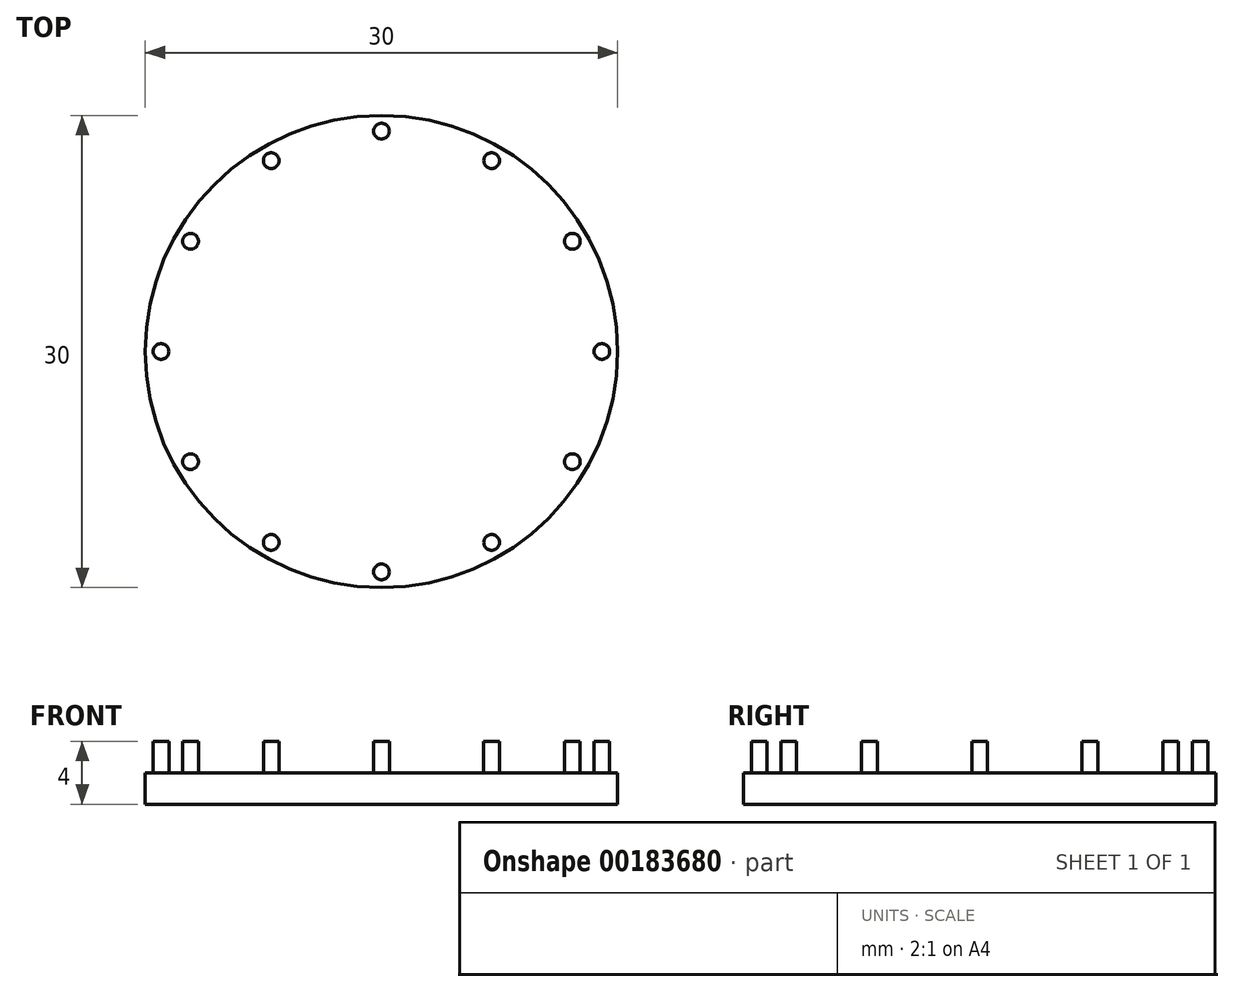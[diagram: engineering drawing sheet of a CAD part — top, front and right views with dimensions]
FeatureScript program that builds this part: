
annotation { "Feature Type Name" : "Feature", "Feature Type Description" : "" }
export const myFeature = defineFeature(function(context is Context, id is Id, definition is map)
    precondition{}
    {
        {
            var Q0;
            Q0=qCreatedBy(makeId("Top.planeOp"),FACE);
            var sketch = newSketch(context, id + "F0", { "sketchPlane" : qUnion([Q0])});
            skCircle(sketch, "E0", {"center": v(0, 0) * mm, "radius": 15 * mm});
            skSolve(sketch);
        }
        {
            var Q0;
            Q0 = qSketchRegion(id + "F0", true);
            extrude(context, id + "F1", {"entities" : qUnion([Q0]), "depth" : 2 * mm});
        }
        {
            var Q0;
            Q0=makeQuery(id+"F1.opExtrude","CAP_FACE",FACE,{"disambiguationData":[OSD([sQuery(id+"F0.wireOp",EDGE,"E0")])],"isStart":false});
            var sketch = newSketch(context, id + "F2", { "sketchPlane" : qUnion([Q0])});
            skCircle(sketch, "E1", {"center": v(0, 14) * mm, "radius": 0.5 * mm});
            skCircle(sketch, "E2", {"center": v(7, 12.12) * mm, "radius": 0.5 * mm});
            skCircle(sketch, "E3", {"center": v(12.12, 7) * mm, "radius": 0.5 * mm});
            skCircle(sketch, "E4", {"center": v(14, 0) * mm, "radius": 0.5 * mm});
            skCircle(sketch, "E5", {"center": v(12.12, -7) * mm, "radius": 0.5 * mm});
            skCircle(sketch, "E6", {"center": v(7, -12.12) * mm, "radius": 0.5 * mm});
            skCircle(sketch, "E7", {"center": v(0, -14) * mm, "radius": 0.5 * mm});
            skCircle(sketch, "E8", {"center": v(-7, -12.12) * mm, "radius": 0.5 * mm});
            skCircle(sketch, "E9", {"center": v(-12.12, -7) * mm, "radius": 0.5 * mm});
            skCircle(sketch, "E10", {"center": v(-14, 0) * mm, "radius": 0.5 * mm});
            skCircle(sketch, "E11", {"center": v(-12.12, 7) * mm, "radius": 0.5 * mm});
            skCircle(sketch, "E12", {"center": v(-7, 12.12) * mm, "radius": 0.5 * mm});
            skCircle(sketch, "E13", {"center": v(0, 0) * mm, "radius": 14 * mm, "construction": true});
            skLineSegment(sketch, "E14", {"start": v(7, 12.12) * mm, "end": v(-7, -12.12) * mm, "construction": true});
            skLineSegment(sketch, "E15", {"start": v(12.12, 7) * mm, "end": v(-12.12, -7) * mm, "construction": true});
            skLineSegment(sketch, "E16", {"start": v(12.12, -7) * mm, "end": v(-12.12, 7) * mm, "construction": true});
            skLineSegment(sketch, "E17", {"start": v(7, -12.12) * mm, "end": v(-7, 12.12) * mm, "construction": true});
            skLineSegment(sketch, "E18", {"start": v(0, -14) * mm, "end": v(0, 14) * mm, "construction": true});
            skLineSegment(sketch, "E19", {"start": v(14, 0) * mm, "end": v(-14, 0) * mm, "construction": true});
            skSolve(sketch);
        }
        {
            var Q0;
            Q0 = qSketchRegion(id + "F2", true);
            extrude(context, id + "F3", {"entities" : qUnion([Q0]), "operationType" : NewBodyOperationType.ADD, "depth" : 2 * mm});
        }
    });
